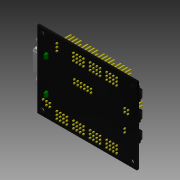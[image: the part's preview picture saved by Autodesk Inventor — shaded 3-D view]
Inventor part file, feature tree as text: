
AUTODESK INVENTOR PART (.ipt)
format: ipt  version: 2015 (Build 190159000, 159)  size: 2,522,112 bytes
history: native  units: mm
features: other x156, imported_body x155, sketch x1
ambient origin geometry x8: Origin, YZ Plane, XZ Plane, XY Plane, X Axis, Y Axis, Z Axis, Center Point
bodies: Body1 (feature_tree), Body2 (feature_tree), Body3 (feature_tree), Body4 (feature_tree), Body5 (feature_tree), Body6 (feature_tree), Body7 (feature_tree), Body8 (feature_tree), Body9 (feature_tree), Body10 (feature_tree), Body11 (feature_tree), Body12 (feature_tree), Body13 (feature_tree), Body14 (feature_tree), Body15 (feature_tree), Body16 (feature_tree), Body17 (feature_tree), Body18 (feature_tree), Body19 (feature_tree), Body20 (feature_tree), Body21 (feature_tree), Body22 (feature_tree), Body23 (feature_tree), Body24 (feature_tree), Body25 (feature_tree), Body26 (feature_tree), Body27 (feature_tree), Body28 (feature_tree), Body29 (feature_tree), Body30 (feature_tree), Body31 (feature_tree), Body32 (feature_tree), Body33 (feature_tree), Body34 (feature_tree), Body35 (feature_tree), Body36 (feature_tree), Body37 (feature_tree), Body38 (feature_tree), Body39 (feature_tree), Body40 (feature_tree), Body41 (feature_tree), Body42 (feature_tree), Body43 (feature_tree), Body44 (feature_tree), Body45 (feature_tree), Body46 (feature_tree), Body47 (feature_tree), Body48 (feature_tree), Body49 (feature_tree), Body50 (feature_tree), Body51 (feature_tree), Body52 (feature_tree), Body53 (feature_tree), Body54 (feature_tree), Body55 (feature_tree), Body56 (feature_tree), Body57 (feature_tree), Body58 (feature_tree), Body59 (feature_tree), Body60 (feature_tree), Body61 (feature_tree), Body62 (feature_tree), Body63 (feature_tree), Body64 (feature_tree), Body65 (feature_tree), Body66 (feature_tree), Body67 (feature_tree), Body68 (feature_tree), Body69 (feature_tree), Body70 (feature_tree), Body71 (feature_tree), Body72 (feature_tree), Body73 (feature_tree), Body74 (feature_tree), Body75 (feature_tree), Body76 (feature_tree), Body77 (feature_tree), Body78 (feature_tree), Body79 (feature_tree), Body80 (feature_tree), Body81 (feature_tree), Body82 (feature_tree), Body83 (feature_tree), Body84 (feature_tree), Body85 (feature_tree), Body86 (feature_tree), Body87 (feature_tree), Body88 (feature_tree), Body89 (feature_tree), Body90 (feature_tree), Body91 (feature_tree), Body92 (feature_tree), Body93 (feature_tree), Body94 (feature_tree), Body95 (feature_tree), Body96 (feature_tree), Body97 (feature_tree), Body98 (feature_tree), Body99 (feature_tree), Body100 (feature_tree), Body101 (feature_tree), Body102 (feature_tree), Body103 (feature_tree), Body104 (feature_tree), Body105 (feature_tree), Body106 (feature_tree), Body107 (feature_tree), Body108 (feature_tree), Body109 (feature_tree), Body110 (feature_tree), Body111 (feature_tree), Body112 (feature_tree), Body113 (feature_tree), Body114 (feature_tree), Body115 (feature_tree), Body116 (feature_tree), Body117 (feature_tree), Body118 (feature_tree), Body119 (feature_tree), Body120 (feature_tree), Body121 (feature_tree), Body122 (feature_tree), Body123 (feature_tree), Body124 (feature_tree), Body125 (feature_tree), Body126 (feature_tree), Body127 (feature_tree), Body128 (feature_tree), Body129 (feature_tree), Body130 (feature_tree), Body131 (feature_tree), Body132 (feature_tree), Body133 (feature_tree), Body134 (feature_tree), Body135 (feature_tree), Body136 (feature_tree), Body137 (feature_tree), Body138 (feature_tree), Body139 (feature_tree), Body140 (feature_tree), Body141 (feature_tree), Body142 (feature_tree), Body143 (feature_tree), Body144 (feature_tree), Body145 (feature_tree), Body146 (feature_tree), Body147 (feature_tree), Body148 (feature_tree), Body149 (feature_tree), Body150 (feature_tree), Body151 (feature_tree), Body152 (feature_tree), Body153 (feature_tree), Body154 (feature_tree), Body155 (feature_tree)
feature tree (312):
  other  "ssc-32"
  other  "ssc-321"
  sketch  "Sketch1"  dims[d0=69.0mm d1=50.8mm]
  other  "ssc-32_1"
  other  "ssc-32_2"
  other  "ssc-32_3"
  other  "ssc-32_4"
  other  "ssc-32_5"
  other  "ssc-32_6"
  other  "ssc-32_7"
  other  "ssc-32_8"
  other  "ssc-32_9"
  other  "ssc-32_10"
  other  "ssc-32_11"
  other  "ssc-32_12"
  other  "ssc-32_13"
  other  "ssc-32_14"
  other  "ssc-32_15"
  other  "ssc-32_16"
  other  "ssc-32_17"
  other  "ssc-32_18"
  other  "ssc-32_19"
  other  "ssc-32_20"
  other  "ssc-32_21"
  other  "ssc-32_22"
  other  "ssc-32_23"
  other  "ssc-32_24"
  other  "ssc-32_25"
  other  "ssc-32_26"
  other  "ssc-32_27"
  other  "ssc-32_28"
  other  "ssc-32_29"
  other  "ssc-32_30"
  other  "ssc-32_31"
  other  "ssc-32_32"
  other  "ssc-32_33"
  other  "ssc-32_34"
  other  "ssc-32_35"
  other  "ssc-32_36"
  other  "ssc-32_37"
  other  "ssc-32_38"
  other  "ssc-32_39"
  other  "ssc-32_40"
  other  "ssc-32_41"
  other  "ssc-32_42"
  other  "ssc-32_43"
  other  "ssc-32_44"
  other  "ssc-32_45"
  other  "ssc-32_46"
  other  "ssc-32_47"
  other  "ssc-32_48"
  other  "ssc-32_49"
  other  "ssc-32_50"
  other  "ssc-32_51"
  other  "ssc-32_52"
  other  "ssc-32_53"
  other  "ssc-32_54"
  other  "ssc-32_55"
  other  "ssc-32_56"
  other  "ssc-32_57"
  other  "ssc-32_58"
  other  "ssc-32_59"
  other  "ssc-32_60"
  other  "ssc-32_61"
  other  "ssc-32_62"
  other  "ssc-32_63"
  other  "ssc-32_64"
  other  "ssc-32_65"
  other  "ssc-32_66"
  other  "ssc-32_67"
  other  "ssc-32_68"
  other  "ssc-32_69"
  other  "ssc-32_70"
  other  "ssc-32_71"
  other  "ssc-32_72"
  other  "ssc-32_73"
  other  "ssc-32_74"
  other  "ssc-32_75"
  other  "ssc-32_76"
  other  "ssc-32_77"
  other  "ssc-32_78"
  other  "ssc-32_79"
  other  "ssc-32_80"
  other  "ssc-32_81"
  other  "ssc-32_82"
  other  "ssc-32_83"
  other  "ssc-32_84"
  other  "ssc-32_85"
  other  "ssc-32_86"
  other  "ssc-32_87"
  other  "ssc-32_88"
  other  "ssc-32_89"
  other  "ssc-32_90"
  other  "ssc-32_91"
  other  "ssc-32_92"
  other  "ssc-32_93"
  other  "ssc-32_94"
  other  "ssc-32_95"
  other  "ssc-32_96"
  other  "ssc-32_97"
  other  "ssc-32_98"
  other  "ssc-32_99"
  other  "ssc-32_100"
  other  "ssc-32_101"
  other  "ssc-32_102"
  other  "ssc-32_103"
  other  "ssc-32_104"
  other  "ssc-32_105"
  other  "ssc-32_106"
  other  "ssc-32_107"
  other  "ssc-32_108"
  other  "ssc-32_109"
  other  "ssc-32_110"
  other  "ssc-32_111"
  other  "ssc-32_112"
  other  "ssc-32_113"
  other  "ssc-32_114"
  other  "ssc-32_115"
  other  "ssc-32_116"
  other  "ssc-32_117"
  other  "ssc-32_118"
  other  "ssc-32_119"
  other  "ssc-32_120"
  other  "ssc-32_121"
  other  "ssc-32_122"
  other  "ssc-32_123"
  other  "ssc-32_124"
  other  "ssc-32_125"
  other  "ssc-32_126"
  other  "ssc-32_127"
  other  "ssc-32_128"
  other  "ssc-32_129"
  other  "ssc-32_130"
  other  "ssc-32_131"
  other  "ssc-32_132"
  other  "ssc-32_133"
  other  "ssc-32_134"
  other  "ssc-32_135"
  other  "ssc-32_136"
  other  "ssc-32_137"
  other  "ssc-32_138"
  other  "ssc-32_139"
  other  "ssc-32_140"
  other  "ssc-32_141"
  other  "ssc-32_142"
  other  "ssc-32_143"
  other  "ssc-32_144"
  other  "ssc-32_145"
  other  "ssc-32_146"
  other  "ssc-32_147"
  other  "ssc-32_148"
  other  "ssc-32_149"
  other  "ssc-32_150"
  other  "ssc-32_151"
  other  "ssc-32_152"
  other  "ssc-32_153"
  other  "ssc-32_154"
  imported_body  "Base1"
  imported_body  "Base2"
  imported_body  "Base3"
  imported_body  "Base4"
  imported_body  "Base5"
  imported_body  "Base6"
  imported_body  "Base7"
  imported_body  "Base8"
  imported_body  "Base9"
  imported_body  "Base10"
  imported_body  "Base11"
  imported_body  "Base12"
  imported_body  "Base13"
  imported_body  "Base14"
  imported_body  "Base15"
  imported_body  "Base16"
  imported_body  "Base17"
  imported_body  "Base18"
  imported_body  "Base19"
  imported_body  "Base20"
  imported_body  "Base21"
  imported_body  "Base22"
  imported_body  "Base23"
  imported_body  "Base24"
  imported_body  "Base25"
  imported_body  "Base26"
  imported_body  "Base27"
  imported_body  "Base28"
  imported_body  "Base29"
  imported_body  "Base30"
  imported_body  "Base31"
  imported_body  "Base32"
  imported_body  "Base33"
  imported_body  "Base34"
  imported_body  "Base35"
  imported_body  "Base36"
  imported_body  "Base37"
  imported_body  "Base38"
  imported_body  "Base39"
  imported_body  "Base40"
  imported_body  "Base41"
  imported_body  "Base42"
  imported_body  "Base43"
  imported_body  "Base44"
  imported_body  "Base45"
  imported_body  "Base46"
  imported_body  "Base47"
  imported_body  "Base48"
  imported_body  "Base49"
  imported_body  "Base50"
  imported_body  "Base51"
  imported_body  "Base52"
  imported_body  "Base53"
  imported_body  "Base54"
  imported_body  "Base55"
  imported_body  "Base56"
  imported_body  "Base57"
  imported_body  "Base58"
  imported_body  "Base59"
  imported_body  "Base60"
  imported_body  "Base61"
  imported_body  "Base62"
  imported_body  "Base63"
  imported_body  "Base64"
  imported_body  "Base65"
  imported_body  "Base66"
  imported_body  "Base67"
  imported_body  "Base68"
  imported_body  "Base69"
  imported_body  "Base70"
  imported_body  "Base71"
  imported_body  "Base72"
  imported_body  "Base73"
  imported_body  "Base74"
  imported_body  "Base75"
  imported_body  "Base76"
  imported_body  "Base77"
  imported_body  "Base78"
  imported_body  "Base79"
  imported_body  "Base80"
  imported_body  "Base81"
  imported_body  "Base82"
  imported_body  "Base83"
  imported_body  "Base84"
  imported_body  "Base85"
  imported_body  "Base86"
  imported_body  "Base87"
  imported_body  "Base88"
  imported_body  "Base89"
  imported_body  "Base90"
  imported_body  "Base91"
  imported_body  "Base92"
  imported_body  "Base93"
  imported_body  "Base94"
  imported_body  "Base95"
  imported_body  "Base96"
  imported_body  "Base97"
  imported_body  "Base98"
  imported_body  "Base99"
  imported_body  "Base100"
  imported_body  "Base101"
  imported_body  "Base102"
  imported_body  "Base103"
  imported_body  "Base104"
  imported_body  "Base105"
  imported_body  "Base106"
  imported_body  "Base107"
  imported_body  "Base108"
  imported_body  "Base109"
  imported_body  "Base110"
  imported_body  "Base111"
  imported_body  "Base112"
  imported_body  "Base113"
  imported_body  "Base114"
  imported_body  "Base115"
  imported_body  "Base116"
  imported_body  "Base117"
  imported_body  "Base118"
  imported_body  "Base119"
  imported_body  "Base120"
  imported_body  "Base121"
  imported_body  "Base122"
  imported_body  "Base123"
  imported_body  "Base124"
  imported_body  "Base125"
  imported_body  "Base126"
  imported_body  "Base127"
  imported_body  "Base128"
  imported_body  "Base129"
  imported_body  "Base130"
  imported_body  "Base131"
  imported_body  "Base132"
  imported_body  "Base133"
  imported_body  "Base134"
  imported_body  "Base135"
  imported_body  "Base136"
  imported_body  "Base137"
  imported_body  "Base138"
  imported_body  "Base139"
  imported_body  "Base140"
  imported_body  "Base141"
  imported_body  "Base142"
  imported_body  "Base143"
  imported_body  "Base144"
  imported_body  "Base145"
  imported_body  "Base146"
  imported_body  "Base147"
  imported_body  "Base148"
  imported_body  "Base149"
  imported_body  "Base150"
  imported_body  "Base151"
  imported_body  "Base152"
  imported_body  "Base153"
  imported_body  "Base154"
  imported_body  "Base155"
